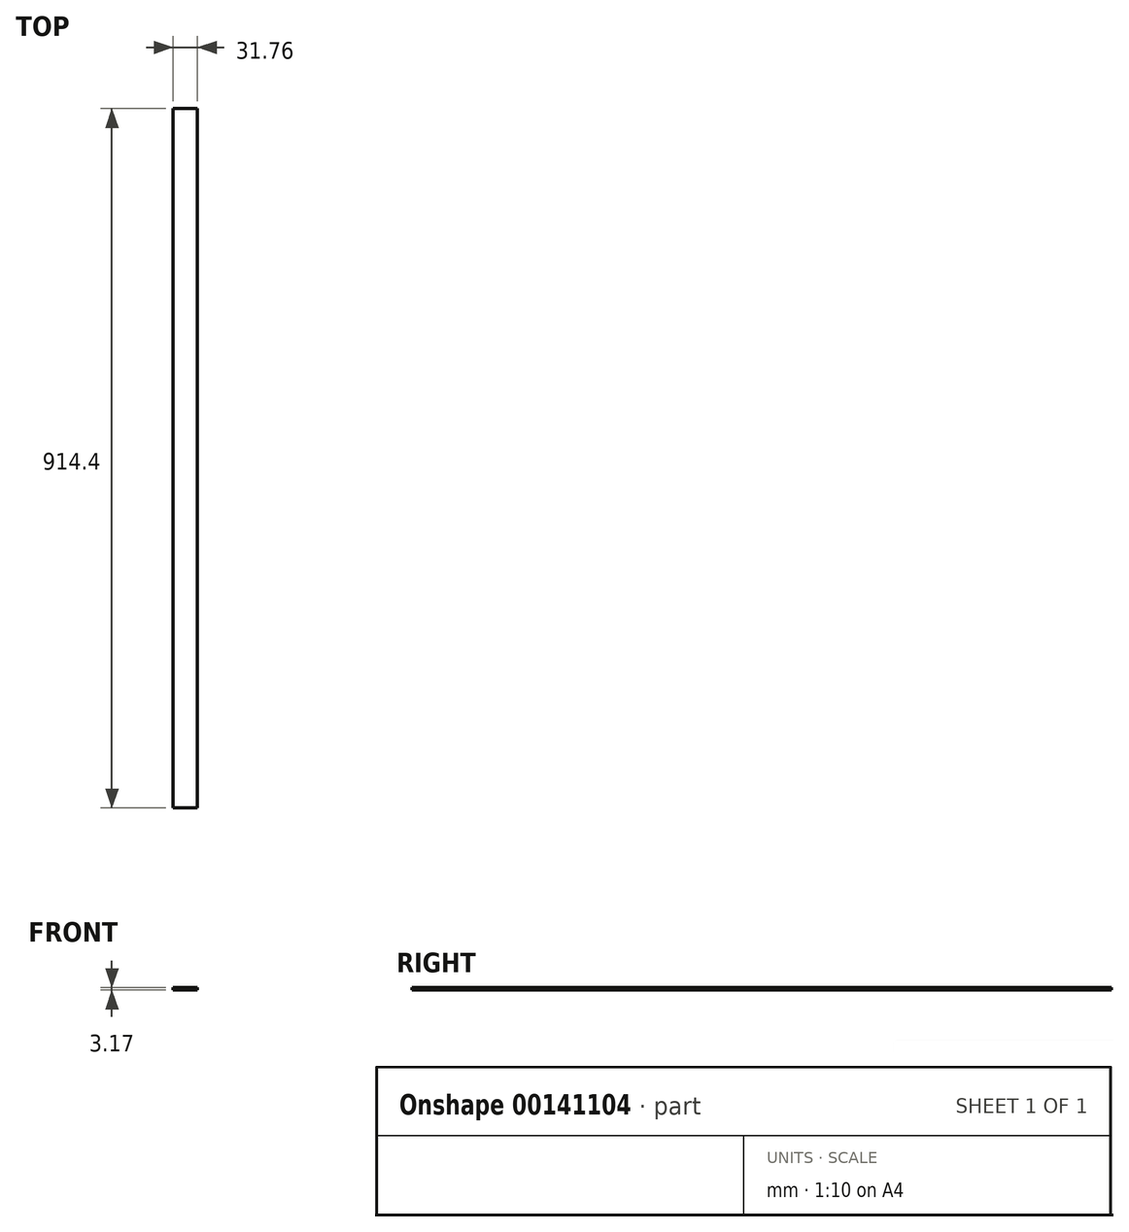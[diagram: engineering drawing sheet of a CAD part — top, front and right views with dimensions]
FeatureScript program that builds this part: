
annotation { "Feature Type Name" : "Feature", "Feature Type Description" : "" }
export const myFeature = defineFeature(function(context is Context, id is Id, definition is map)
    precondition{}
    {
        {
            var Q0;
            Q0=qCreatedBy(makeId("Front.planeOp"),FACE);
            var sketch = newSketch(context, id + "F0", { "sketchPlane" : qUnion([Q0])});
            skLineSegment(sketch, "E0.bottom", {"start": v(-15.88, 0) * mm, "end": v(15.88, 0) * mm});
            skLineSegment(sketch, "E0.top", {"start": v(-15.88, -3.17) * mm, "end": v(15.88, -3.18) * mm});
            skLineSegment(sketch, "E0.left", {"start": v(-15.88, 0) * mm, "end": v(-15.88, -3.17) * mm});
            skLineSegment(sketch, "E0.right", {"start": v(15.88, 0) * mm, "end": v(15.88, -3.17) * mm});
            skSolve(sketch);
        }
        {
            var Q0;
            Q0 = qSketchRegion(id + "F0", true);
            extrude(context, id + "F1", {"entities" : qUnion([Q0]), "depth" : 914.4 * mm});
        }
    });
